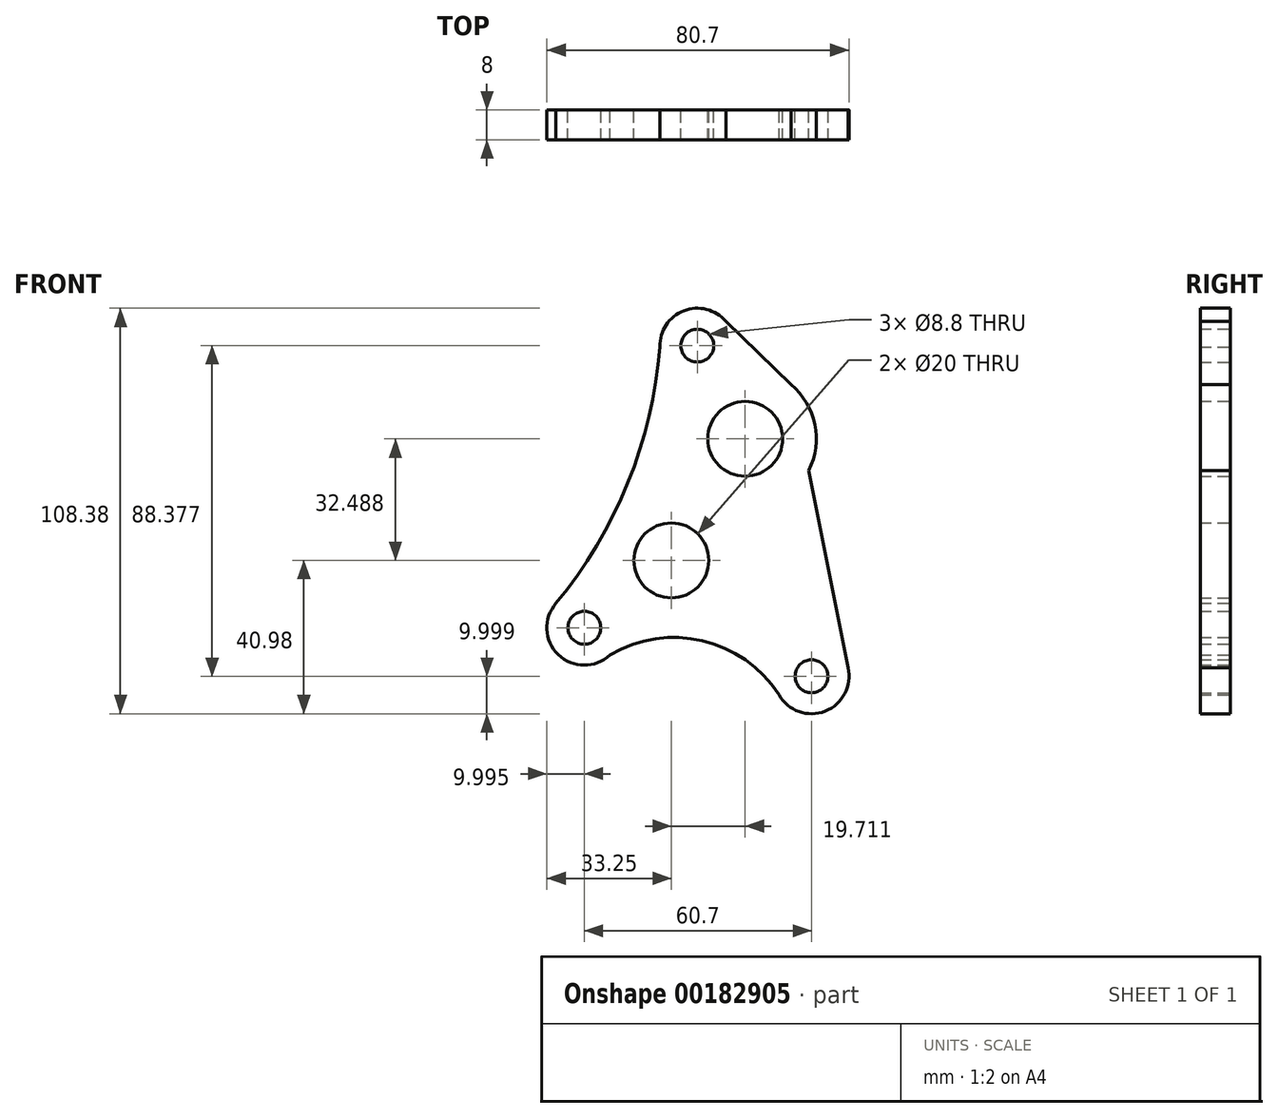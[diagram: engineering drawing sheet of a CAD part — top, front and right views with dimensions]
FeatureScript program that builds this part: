
annotation { "Feature Type Name" : "Feature", "Feature Type Description" : "" }
export const myFeature = defineFeature(function(context is Context, id is Id, definition is map)
    precondition{}
    {
        {
            var Q0;
            Q0=qCreatedBy(makeId("Front.planeOp"),FACE);
            var sketch = newSketch(context, id + "F0", { "sketchPlane" : qUnion([Q0])});
            skCircle(sketch, "E0", {"center": v(0, 0) * mm, "radius": 10 * mm});
            skCircle(sketch, "E1", {"center": v(19.71, 32.49) * mm, "radius": 10 * mm});
            skCircle(sketch, "E2", {"center": v(-23.25, -17.99) * mm, "radius": 4.4 * mm});
            skCircle(sketch, "E3", {"center": v(37.45, -30.98) * mm, "radius": 4.4 * mm});
            skCircle(sketch, "E4", {"center": v(6.92, 57.4) * mm, "radius": 4.4 * mm});
            skArc(sketch, "E5", {"start": v(14.54, 63.87) * mm, "mid": v(3.32, 66.73) * mm, "end": v(-3.07, 57.07) * mm});
            skArc(sketch, "E6", {"start": v(-30.83, -11.46) * mm, "mid": v(-30.2, -25.19) * mm, "end": v(-16.46, -25.32) * mm});
            skArc(sketch, "E7", {"start": v(28.75, -35.92) * mm, "mid": v(41.11, -40.28) * mm, "end": v(47.17, -28.66) * mm});
            skArc(sketch, "E8", {"start": v(36.71, 24.01) * mm, "mid": v(38.32, 36.34) * mm, "end": v(31.95, 47.02) * mm});
            skLineSegment(sketch, "E9", {"start": v(36.71, 24.01) * mm, "end": v(47.17, -28.66) * mm});
            skArc(sketch, "E10", {"start": v(28.75, -35.92) * mm, "mid": v(8.29, -21.48) * mm, "end": v(-16.46, -25.32) * mm});
            skLineSegment(sketch, "E11", {"start": v(14.54, 63.87) * mm, "end": v(31.95, 47.02) * mm});
            skArc(sketch, "E12", {"start": v(-30.83, -11.46) * mm, "mid": v(-11.64, 20.66) * mm, "end": v(-3.07, 57.07) * mm});
            skSolve(sketch);
        }
        {
            var Q0;
            Q0=makeQuery(id+"F0.imprint","IMPRINT",FACE,{"disambiguationData":[TD([[makeQuery(id+"F0.imprint","IMPRINT",EDGE,{"derivedFrom":sQuery(id+"F0.wireOp",EDGE,"WjMIIAeg-OMzP-qFG7-jeDR-DLkIqQscwrKQ")}),-1.0]])]});
            var Q1;
            Q1=makeQuery(id+"F0.imprint","IMPRINT",FACE,{"disambiguationData":[TD([[makeQuery(id+"F0.imprint","IMPRINT",EDGE,{"derivedFrom":sQuery(id+"F0.wireOp",EDGE,"gCQXX55Q-UbVh-VfNQ-s7oq-DzqNekvmLReg")}),-1.0]])]});
            var Q2;
            Q2=makeQuery(id+"F0.imprint","IMPRINT",FACE,{"disambiguationData":[TD([[makeQuery(id+"F0.imprint","IMPRINT",EDGE,{"derivedFrom":sQuery(id+"F0.wireOp",EDGE,"E0")}),-1.0]])]});
            var Q3;
            Q3=makeQuery(id+"F0.imprint","IMPRINT",FACE,{"disambiguationData":[TD([[makeQuery(id+"F0.imprint","IMPRINT",EDGE,{"derivedFrom":sQuery(id+"F0.wireOp",EDGE,"c329502a-a4c5-4b6a-9065-4b2351631a8a")}),-1.0]])]});
            var Q4;
            Q4=makeQuery(id+"F0.imprint","IMPRINT",FACE,{"disambiguationData":[TD([[makeQuery(id+"F0.imprint","IMPRINT",EDGE,{"derivedFrom":sQuery(id+"F0.wireOp",EDGE,"40ccfce5-33a5-4395-8adb-1d8ed9d97b6c")}),-1.0]])]});
            var Q5;
            Q5=makeQuery(id+"F0.imprint","IMPRINT",FACE,{"disambiguationData":[TD([[makeQuery(id+"F0.imprint","IMPRINT",EDGE,{"derivedFrom":sQuery(id+"F0.wireOp",EDGE,"E1")}),-1.0]])]});
            extrude(context, id + "F1", {"entities" : qUnion([Q0, Q1, Q2, Q3, Q4, Q5]), "depth" : 8 * mm});
        }
    });
